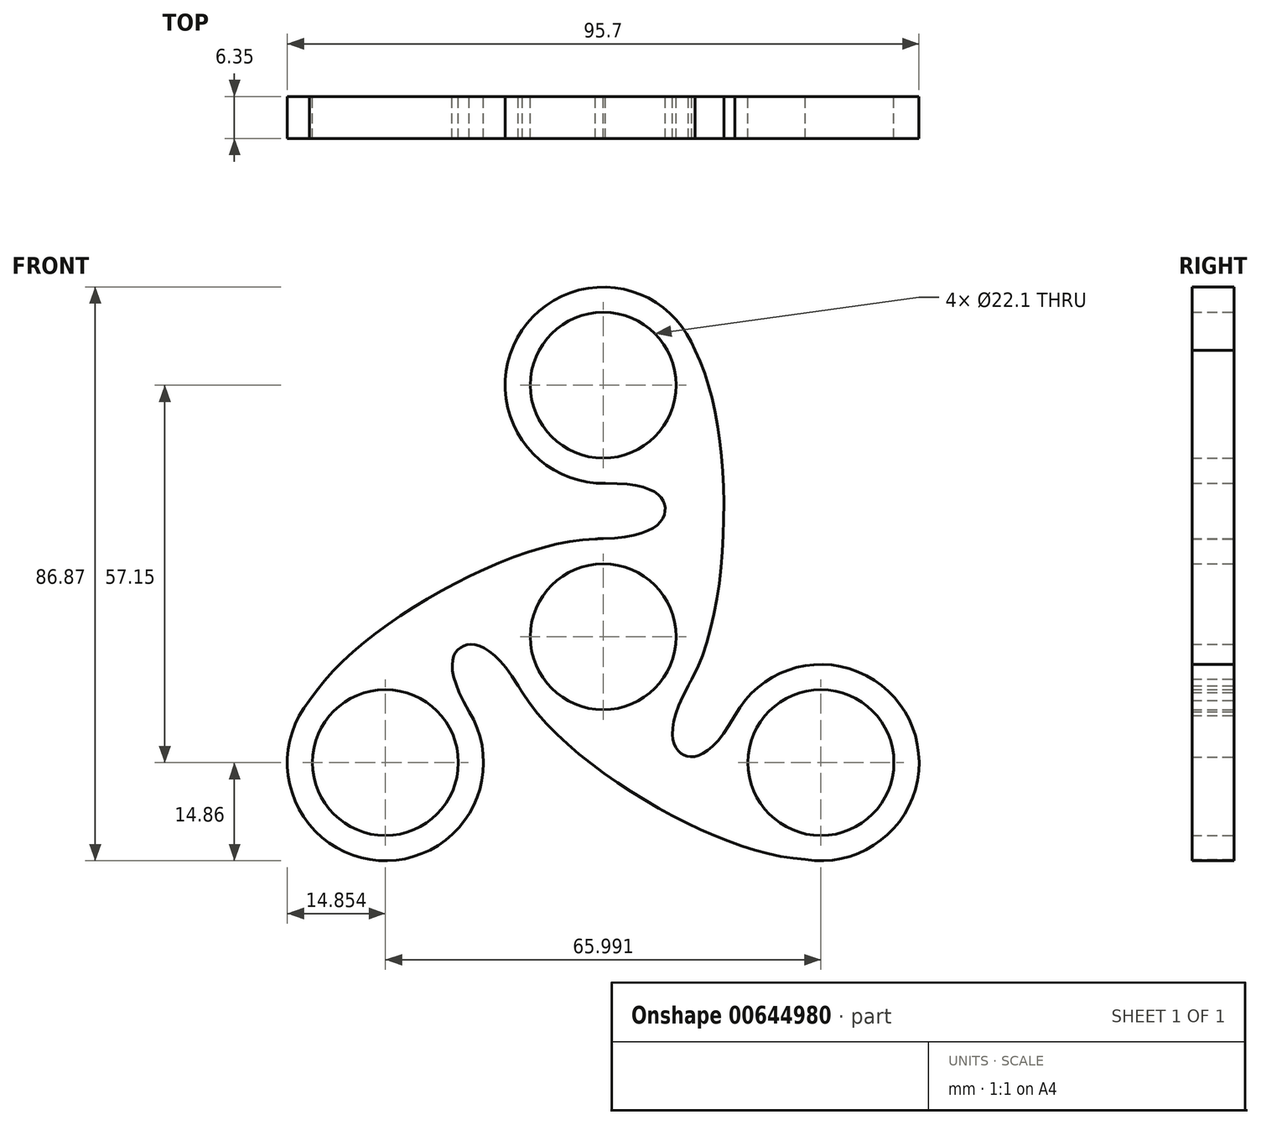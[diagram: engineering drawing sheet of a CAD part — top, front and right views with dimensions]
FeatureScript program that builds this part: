
annotation { "Feature Type Name" : "Feature", "Feature Type Description" : "" }
export const myFeature = defineFeature(function(context is Context, id is Id, definition is map)
    precondition{}
    {
        {
            var Q0;
            Q0=qCreatedBy(makeId("Front.planeOp"),FACE);
            var sketch = newSketch(context, id + "F0", { "sketchPlane" : qUnion([Q0])});
            skCircle(sketch, "E0", {"center": v(0, 0) * mm, "radius": 11.05 * mm});
            skCircle(sketch, "E1", {"center": v(0, 38.1) * mm, "radius": 11.05 * mm});
            skCircle(sketch, "E2", {"center": v(0, 0) * mm, "radius": 14.86 * mm});
            skCircle(sketch, "E3", {"center": v(0, 38.1) * mm, "radius": 14.86 * mm});
            skFitSpline(sketch, "E4", {"points": [v(0, 23.24) * mm, v(9.4, 19.35) * mm, v(0, 14.86) * mm], "startDerivative": vector(44.1, 0.67) * mm, "endDerivative": vector(-43.18, -1.15) * mm});
            skFitSpline(sketch, "E5", {"points": [v(13.9, 43.38) * mm, v(18.27, 19.71) * mm, v(13.41, -6.4) * mm], "startDerivative": vector(18.67, -37.08) * mm, "endDerivative": vector(-20.72, -37.44) * mm});
            skSolve(sketch);
        }
        {
            var Q0;
            Q0 = qSketchRegion(id + "F0", true);
            extrude(context, id + "F1", {"entities" : qUnion([Q0]), "depth" : 6.35 * mm, "offsetDistance" : 25.4 * mm});
        }
        {
            var Q0;
            Q0=makeQuery(id+"F1.opExtrude","SWEPT_BODY",BODY,{"disambiguationData":[OSD([sQuery(id+"F0.wireOp",EDGE,"E0"),sQuery(id+"F0.wireOp",EDGE,"E1"),sQuery(id+"F0.wireOp",EDGE,"E2"),sQuery(id+"F0.wireOp",EDGE,"E3"),sQuery(id+"F0.wireOp",EDGE,"E4"),sQuery(id+"F0.wireOp",EDGE,"E5")])]});
            var Q1;
            Q1=makeQuery(id+"F1.opExtrude","CAP_EDGE",EDGE,{"disambiguationData":[OSD([sQuery(id+"F0.wireOp",EDGE,"E0")])],"isStart":false});
            circularPattern(context, id + "F2", {"operationType" : NewBodyOperationType.ADD, "entities" : qUnion([Q0]), "axis" : qUnion([Q1]), "angle" : 360 * degree, "instanceCount" : 3, "equalSpace" : true});
        }
    });
